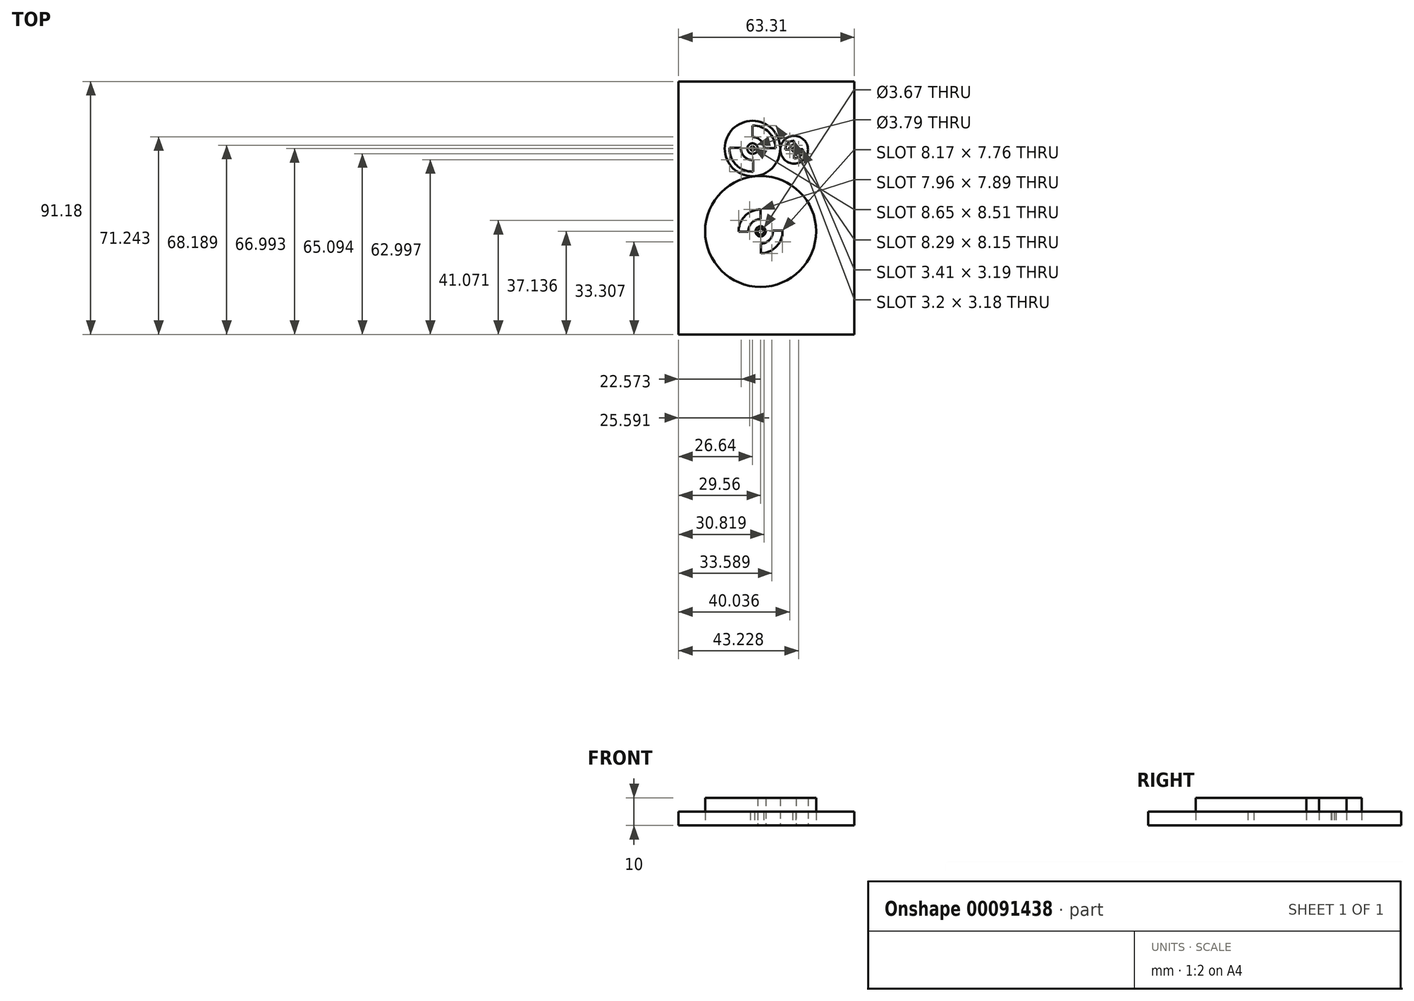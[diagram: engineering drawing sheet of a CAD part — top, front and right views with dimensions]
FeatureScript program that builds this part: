
annotation { "Feature Type Name" : "Feature", "Feature Type Description" : "" }
export const myFeature = defineFeature(function(context is Context, id is Id, definition is map)
    precondition{}
    {
        {
            var Q0;
            Q0=qCreatedBy(makeId("Top.planeOp"),FACE);
            var sketch = newSketch(context, id + "F0", { "sketchPlane" : qUnion([Q0])});
            skCircle(sketch, "E0", {"center": v(-64.92, -13.69) * mm, "radius": 10 * mm});
            skCircle(sketch, "E1", {"center": v(-62, -43.54) * mm, "radius": 20 * mm});
            skCircle(sketch, "E2", {"center": v(-49.93, -14.1) * mm, "radius": 5 * mm});
            skCircle(sketch, "E3", {"center": v(-64.92, -13.69) * mm, "radius": 8.33 * mm});
            skCircle(sketch, "E4", {"center": v(-64.92, -13.69) * mm, "radius": 4.17 * mm});
            skLineSegment(sketch, "E5", {"start": v(-64.89, -9.52) * mm, "end": v(-64.89, -5.36) * mm});
            skLineSegment(sketch, "E6", {"start": v(-73.24, -13.36) * mm, "end": v(-69.08, -13.36) * mm});
            skLineSegment(sketch, "E7", {"start": v(-60.76, -13.51) * mm, "end": v(-56.6, -13.51) * mm});
            skLineSegment(sketch, "E8", {"start": v(-64.73, -17.85) * mm, "end": v(-64.73, -22.01) * mm});
            skCircle(sketch, "E9", {"center": v(-62, -43.54) * mm, "radius": 7.92 * mm});
            skCircle(sketch, "E10", {"center": v(-62, -43.54) * mm, "radius": 4.43 * mm});
            skLineSegment(sketch, "E11", {"start": v(-62.02, -39.12) * mm, "end": v(-62.02, -35.63) * mm});
            skLineSegment(sketch, "E12", {"start": v(-61.85, -47.97) * mm, "end": v(-61.85, -51.46) * mm});
            skLineSegment(sketch, "E13", {"start": v(-57.58, -43.29) * mm, "end": v(-54.09, -43.29) * mm});
            skLineSegment(sketch, "E14", {"start": v(-66.43, -43.59) * mm, "end": v(-69.92, -43.59) * mm});
            skCircle(sketch, "E15", {"center": v(-49.93, -14.1) * mm, "radius": 3.2 * mm});
            skCircle(sketch, "E16", {"center": v(-49.93, -14.1) * mm, "radius": 1.82 * mm});
            skLineSegment(sketch, "E17", {"start": v(-49.93, -12.28) * mm, "end": v(-49.93, -10.9) * mm});
            skLineSegment(sketch, "E18", {"start": v(-49.93, -15.91) * mm, "end": v(-49.93, -17.3) * mm});
            skLineSegment(sketch, "E19", {"start": v(-51.74, -14.08) * mm, "end": v(-53.12, -14.08) * mm});
            skLineSegment(sketch, "E20", {"start": v(-46.74, -13.88) * mm, "end": v(-48.12, -13.88) * mm});
            skCircle(sketch, "E21", {"center": v(-62, -43.54) * mm, "radius": 1.84 * mm});
            skCircle(sketch, "E22", {"center": v(-64.92, -13.69) * mm, "radius": 1.9 * mm});
            skCircle(sketch, "E23", {"center": v(-49.93, -14.1) * mm, "radius": 0.74 * mm});
            skSolve(sketch);
        }
        {
            var Q0;
            {var subQ4=sQuery(id+"F0.wireOp",EDGE,"E0");var subQ5=makeQuery(id+"F0.imprint","INTERSECT",VERTEX,{"derivedFrom":[subQ4,sQuery(id+"F0.wireOp",EDGE,"E1")]});Q0=makeQuery(id+"F0.imprint","IMPRINT",FACE,{"disambiguationData":[TD([[makeQuery(id+"F0.imprint","IMPRINT",EDGE,{"disambiguationData":[TD([[subQ5,-1.0]])],"derivedFrom":subQ4}),1.0]])]});}
            var Q1;
            {var subQ0=sQuery(id+"F0.wireOp",EDGE,"E5");Q1=makeQuery(id+"F0.imprint","IMPRINT",FACE,{"disambiguationData":[TD([[makeQuery(id+"F0.imprint","IMPRINT",EDGE,{"derivedFrom":subQ0}),1.0]])]});}
            var Q2;
            {var subQ0=sQuery(id+"F0.wireOp",EDGE,"E7");Q2=makeQuery(id+"F0.imprint","IMPRINT",FACE,{"disambiguationData":[TD([[makeQuery(id+"F0.imprint","IMPRINT",EDGE,{"derivedFrom":subQ0}),-1.0]])]});}
            var Q3;
            Q3=makeQuery(id+"F0.imprint","IMPRINT",FACE,{"disambiguationData":[TD([[makeQuery(id+"F0.imprint","IMPRINT",EDGE,{"derivedFrom":sQuery(id+"F0.wireOp",EDGE,"E22")}),-1.0]])]});
            var Q4;
            Q4=makeQuery(id+"F0.imprint","IMPRINT",FACE,{"disambiguationData":[TD([[makeQuery(id+"F0.imprint","IMPRINT",EDGE,{"derivedFrom":sQuery(id+"F0.wireOp",EDGE,"E1")}),1.0]])]});
            var Q5;
            {var subQ0=sQuery(id+"F0.wireOp",EDGE,"E11");Q5=makeQuery(id+"F0.imprint","IMPRINT",FACE,{"disambiguationData":[TD([[makeQuery(id+"F0.imprint","IMPRINT",EDGE,{"derivedFrom":subQ0}),-1.0]])]});}
            var Q6;
            {var subQ0=sQuery(id+"F0.wireOp",EDGE,"E12");Q6=makeQuery(id+"F0.imprint","IMPRINT",FACE,{"disambiguationData":[TD([[makeQuery(id+"F0.imprint","IMPRINT",EDGE,{"derivedFrom":subQ0}),-1.0]])]});}
            var Q7;
            Q7=makeQuery(id+"F0.imprint","IMPRINT",FACE,{"disambiguationData":[TD([[makeQuery(id+"F0.imprint","IMPRINT",EDGE,{"derivedFrom":sQuery(id+"F0.wireOp",EDGE,"E21")}),-1.0]])]});
            var Q8;
            Q8=makeQuery(id+"F0.imprint","IMPRINT",FACE,{"disambiguationData":[TD([[makeQuery(id+"F0.imprint","IMPRINT",EDGE,{"derivedFrom":sQuery(id+"F0.wireOp",EDGE,"E2")}),1.0]])]});
            var Q9;
            {var subQ0=sQuery(id+"F0.wireOp",EDGE,"E18");Q9=makeQuery(id+"F0.imprint","IMPRINT",FACE,{"disambiguationData":[TD([[makeQuery(id+"F0.imprint","IMPRINT",EDGE,{"derivedFrom":subQ0}),-1.0]])]});}
            var Q10;
            {var subQ0=sQuery(id+"F0.wireOp",EDGE,"E17");Q10=makeQuery(id+"F0.imprint","IMPRINT",FACE,{"disambiguationData":[TD([[makeQuery(id+"F0.imprint","IMPRINT",EDGE,{"derivedFrom":subQ0}),-1.0]])]});}
            var Q11;
            Q11=makeQuery(id+"F0.imprint","IMPRINT",FACE,{"disambiguationData":[TD([[makeQuery(id+"F0.imprint","IMPRINT",EDGE,{"derivedFrom":sQuery(id+"F0.wireOp",EDGE,"E23")}),-1.0]])]});
            extrude(context, id + "F1", {"entities" : qUnion([Q0, Q1, Q2, Q3, Q4, Q5, Q6, Q7, Q8, Q9, Q10, Q11]), "depth" : 10 * mm});
        }
        {
            var Q0;
            Q0=qCreatedBy(makeId("Top.planeOp"),FACE);
            var sketch = newSketch(context, id + "F2", { "sketchPlane" : qUnion([Q0])});
            skLineSegment(sketch, "E24.bottom", {"start": v(-91.56, 10.5) * mm, "end": v(-28.25, 10.5) * mm});
            skLineSegment(sketch, "E24.top", {"start": v(-91.56, -80.68) * mm, "end": v(-28.25, -80.68) * mm});
            skLineSegment(sketch, "E24.left", {"start": v(-91.56, 10.5) * mm, "end": v(-91.56, -80.68) * mm});
            skLineSegment(sketch, "E24.right", {"start": v(-28.25, 10.5) * mm, "end": v(-28.25, -80.68) * mm});
            skCircle(sketch, "E25", {"center": v(-64.9, -13.69) * mm, "radius": 0.78 * mm});
            skCircle(sketch, "E26", {"center": v(-49.93, -14.1) * mm, "radius": 0.56 * mm});
            skCircle(sketch, "E27", {"center": v(-61.99, -43.65) * mm, "radius": 1.1 * mm});
            skSolve(sketch);
        }
        {
            var Q0;
            Q0=makeQuery(id+"F2.imprint","IMPRINT",FACE,{"disambiguationData":[TD([[makeQuery(id+"F2.imprint","IMPRINT",EDGE,{"derivedFrom":sQuery(id+"F2.wireOp",EDGE,"E24.bottom")}),-1.0]])]});
            extrude(context, id + "F3", {"entities" : qUnion([Q0]), "depth" : 5 * mm});
        }
    });
